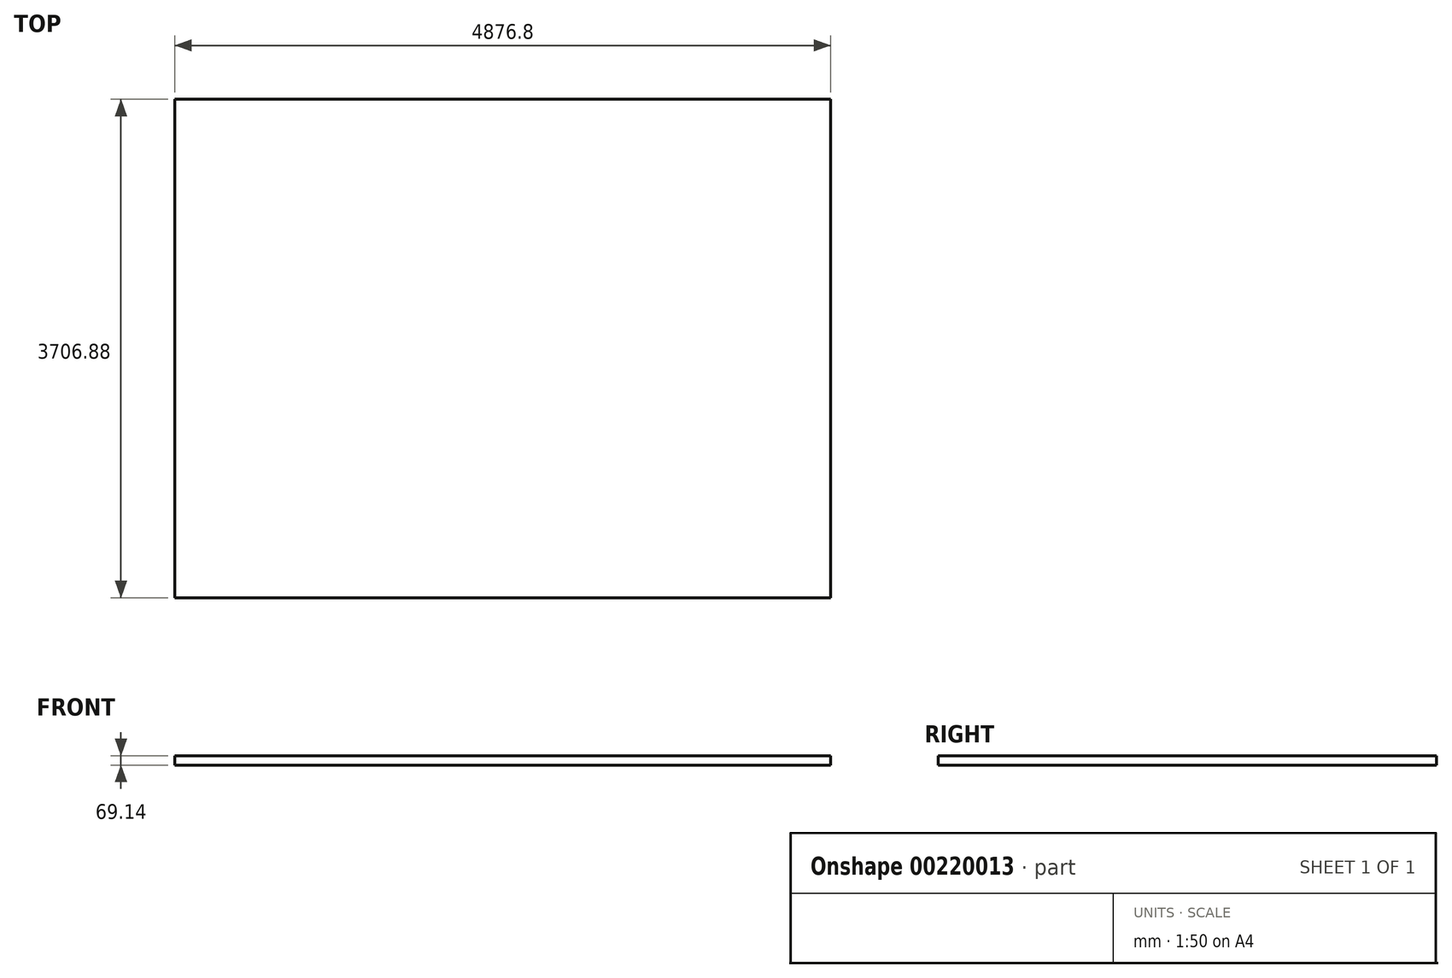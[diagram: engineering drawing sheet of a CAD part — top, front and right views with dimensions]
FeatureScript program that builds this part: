
annotation { "Feature Type Name" : "Feature", "Feature Type Description" : "" }
export const myFeature = defineFeature(function(context is Context, id is Id, definition is map)
    precondition{}
    {
        {
            var Q0;
            Q0=qCreatedBy(makeId("Top.planeOp"),FACE);
            var sketch = newSketch(context, id + "F0", { "sketchPlane" : qUnion([Q0])});
            skLineSegment(sketch, "E0.bottom", {"start": v(0, 0) * mm, "end": v(-4876.8, 0) * mm});
            skLineSegment(sketch, "E0.top", {"start": v(0, -3706.88) * mm, "end": v(-4876.8, -3706.88) * mm});
            skLineSegment(sketch, "E0.left", {"start": v(0, 0) * mm, "end": v(0, -3706.88) * mm});
            skLineSegment(sketch, "E0.right", {"start": v(-4876.8, 0) * mm, "end": v(-4876.8, -3706.88) * mm});
            skSolve(sketch);
        }
        {
            var Q0;
            Q0=makeQuery(id+"F0.imprint","IMPRINT",FACE,{"disambiguationData":[TD([[makeQuery(id+"F0.imprint","IMPRINT",EDGE,{"derivedFrom":sQuery(id+"F0.wireOp",EDGE,"E0.bottom")}),1.0]])]});
            extrude(context, id + "F1", {"entities" : qUnion([Q0]), "depth" : 69.14 * mm});
        }
    });
